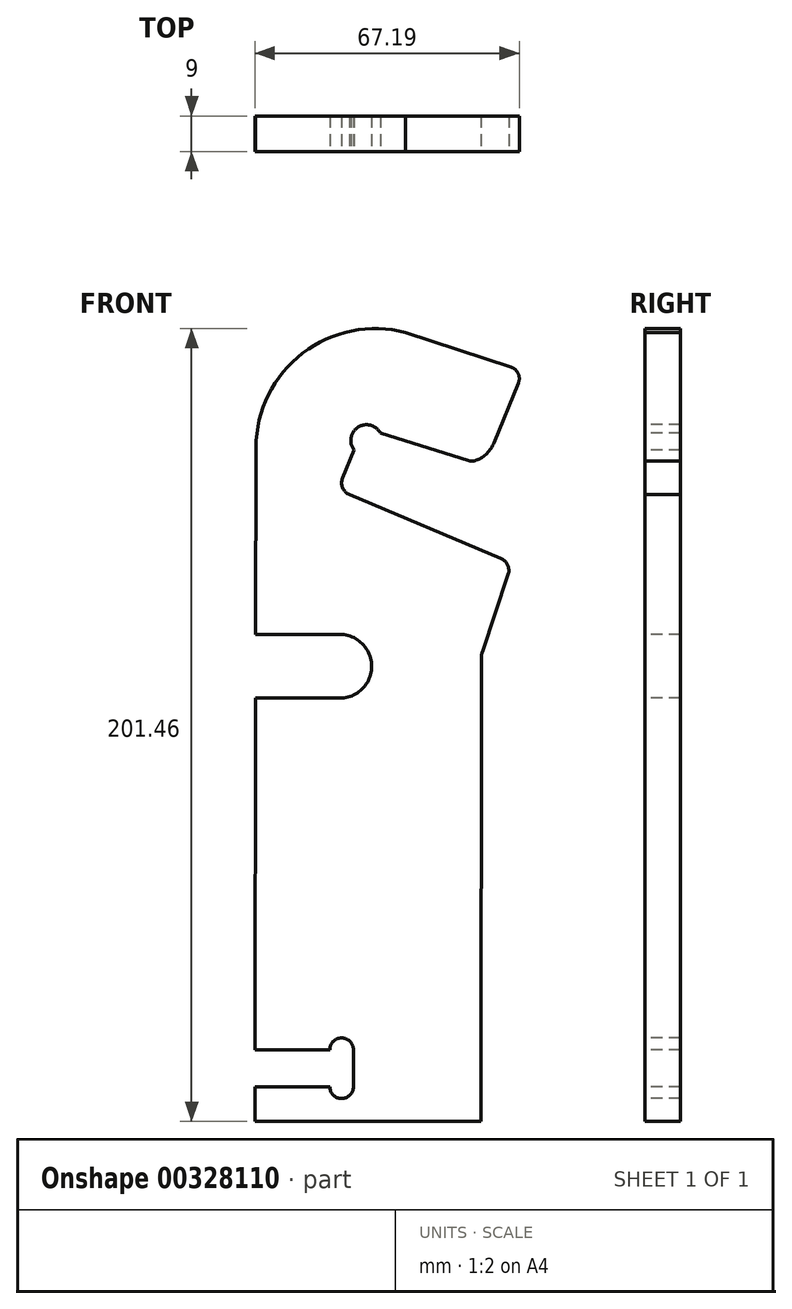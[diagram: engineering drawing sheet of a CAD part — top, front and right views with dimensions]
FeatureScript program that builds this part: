
annotation { "Feature Type Name" : "Feature", "Feature Type Description" : "" }
export const myFeature = defineFeature(function(context is Context, id is Id, definition is map)
    precondition{}
    {
        {
            var Q0;
            Q0=qCreatedBy(makeId("Front.planeOp"),FACE);
            var sketch = newSketch(context, id + "F0", { "sketchPlane" : qUnion([Q0])});
            skArc(sketch, "E0", {"start": v(12.26, 34.16) * mm, "mid": v(20.35, 26.05) * mm, "end": v(12.24, 17.96) * mm});
            skLineSegment(sketch, "E1", {"start": v(12.24, 17.96) * mm, "end": v(-9.16, 17.99) * mm});
            skLineSegment(sketch, "E2", {"start": v(-9.16, 17.99) * mm, "end": v(-9.32, -89.52) * mm});
            skLineSegment(sketch, "E3", {"start": v(-9.32, -89.52) * mm, "end": v(48.13, -89.6) * mm});
            skLineSegment(sketch, "E4", {"start": v(48.13, -89.6) * mm, "end": v(48.3, 28.7) * mm});
            skArc(sketch, "E5", {"start": v(48.3, 28.7) * mm, "mid": v(48.34, 29.2) * mm, "end": v(48.46, 29.7) * mm});
            skLineSegment(sketch, "E6", {"start": v(48.46, 29.7) * mm, "end": v(55.05, 49.38) * mm});
            skArc(sketch, "E7", {"start": v(55.05, 49.38) * mm, "mid": v(54.93, 51.79) * mm, "end": v(53.2, 53.47) * mm});
            skLineSegment(sketch, "E8", {"start": v(53.2, 53.47) * mm, "end": v(14.74, 69.69) * mm});
            skArc(sketch, "E9", {"start": v(14.74, 69.69) * mm, "mid": v(13, 71.4) * mm, "end": v(12.98, 73.86) * mm});
            skLineSegment(sketch, "E10", {"start": v(12.98, 73.86) * mm, "end": v(15.89, 81.01) * mm});
            skArc(sketch, "E11", {"start": v(15.89, 81.01) * mm, "mid": v(16.94, 86.81) * mm, "end": v(22.63, 85.27) * mm});
            skLineSegment(sketch, "E12", {"start": v(22.63, 85.27) * mm, "end": v(45.01, 78.33) * mm});
            skArc(sketch, "E13", {"start": v(45.01, 78.33) * mm, "mid": v(46.01, 78.2) * mm, "end": v(47, 78.4) * mm});
            skArc(sketch, "E14", {"start": v(47, 78.4) * mm, "mid": v(49.69, 80.16) * mm, "end": v(51.47, 82.83) * mm});
            skLineSegment(sketch, "E15", {"start": v(51.47, 82.83) * mm, "end": v(57.65, 98.06) * mm});
            skArc(sketch, "E16", {"start": v(57.65, 98.06) * mm, "mid": v(57.6, 100.45) * mm, "end": v(55.81, 102.04) * mm});
            skLineSegment(sketch, "E17", {"start": v(55.81, 102.04) * mm, "end": v(29, 110.89) * mm});
            skArc(sketch, "E18", {"start": v(29, 110.89) * mm, "mid": v(2.86, 105.6) * mm, "end": v(-9.04, 81.71) * mm});
            skLineSegment(sketch, "E19", {"start": v(-9.04, 81.71) * mm, "end": v(-9.14, 34.19) * mm});
            skLineSegment(sketch, "E20", {"start": v(-9.14, 34.19) * mm, "end": v(12.26, 34.16) * mm});
            skLineSegment(sketch, "E21", {"start": v(-19.3, -76.73) * mm, "end": v(-19.3, -75.33) * mm});
            skArc(sketch, "E22", {"start": v(-19.3, -75.33) * mm, "mid": v(-18.12, -72.5) * mm, "end": v(-15.3, -71.33) * mm});
            skLineSegment(sketch, "E23", {"start": v(-15.3, -71.33) * mm, "end": v(9.74, -71.37) * mm});
            skArc(sketch, "E24", {"start": v(9.74, -71.37) * mm, "mid": v(12.75, -68.37) * mm, "end": v(15.74, -71.38) * mm});
            skLineSegment(sketch, "E25", {"start": v(15.74, -71.38) * mm, "end": v(15.73, -80.78) * mm});
            skArc(sketch, "E26", {"start": v(15.73, -80.78) * mm, "mid": v(12.72, -83.77) * mm, "end": v(9.73, -80.77) * mm});
            skLineSegment(sketch, "E27", {"start": v(9.73, -80.77) * mm, "end": v(-15.3, -80.73) * mm});
            skArc(sketch, "E28", {"start": v(-15.3, -80.73) * mm, "mid": v(-18.13, -79.56) * mm, "end": v(-19.3, -76.73) * mm});
            skLineSegment(sketch, "E29", {"start": v(39.17, -62.62) * mm, "end": v(30.17, -62.6) * mm});
            skArc(sketch, "E30", {"start": v(30.17, -62.6) * mm, "mid": v(27, -59.42) * mm, "end": v(30.18, -56.25) * mm});
            skLineSegment(sketch, "E31", {"start": v(30.18, -56.25) * mm, "end": v(30.3, 31.05) * mm});
            skArc(sketch, "E32", {"start": v(30.3, 31.05) * mm, "mid": v(27.13, 34.23) * mm, "end": v(30.31, 37.4) * mm});
            skLineSegment(sketch, "E33", {"start": v(30.31, 37.4) * mm, "end": v(39.31, 37.38) * mm});
            skArc(sketch, "E34", {"start": v(39.31, 37.38) * mm, "mid": v(42.48, 34.2) * mm, "end": v(39.3, 31.03) * mm});
            skLineSegment(sketch, "E35", {"start": v(39.3, 31.03) * mm, "end": v(39.18, -56.27) * mm});
            skArc(sketch, "E36", {"start": v(39.18, -56.27) * mm, "mid": v(42.35, -59.45) * mm, "end": v(39.17, -62.62) * mm});
            skSolve(sketch);
        }
        {
            var Q0;
            Q0=makeQuery(id+"F0.imprint","IMPRINT",FACE,{"disambiguationData":[TD([[makeQuery(id+"F0.imprint","IMPRINT",EDGE,{"derivedFrom":sQuery(id+"F0.wireOp",EDGE,"E29")}),-1.0]])]});
            var Q1;
            {var subQ0=sQuery(id+"F0.wireOp",EDGE,"E24");Q1=makeQuery(id+"F0.imprint","IMPRINT",FACE,{"disambiguationData":[TD([[makeQuery(id+"F0.imprint","IMPRINT",EDGE,{"derivedFrom":subQ0}),-1.0]])]});}
            var Q2;
            Q2=makeQuery(id+"F0.imprint","IMPRINT",FACE,{"disambiguationData":[TD([[makeQuery(id+"F0.imprint","IMPRINT",EDGE,{"derivedFrom":sQuery(id+"F0.wireOp",EDGE,"E0")}),1.0]])]});
            extrude(context, id + "F1", {"entities" : qUnion([Q0, Q1, Q2]), "oppositeDirection" : true, "depth" : 18 * mm});
        }
        {
            var Q0;
            {var subQ0=sQuery(id+"F0.wireOp",EDGE,"E24");Q0=makeQuery(id+"F0.imprint","IMPRINT",FACE,{"disambiguationData":[TD([[makeQuery(id+"F0.imprint","IMPRINT",EDGE,{"derivedFrom":subQ0}),-1.0]])]});}
            var Q1;
            Q1=makeQuery(id+"F0.imprint","IMPRINT",FACE,{"disambiguationData":[TD([[makeQuery(id+"F0.imprint","IMPRINT",EDGE,{"derivedFrom":sQuery(id+"F0.wireOp",EDGE,"E29")}),-1.0]])]});
            extrude(context, id + "F2", {"entities" : qUnion([Q0, Q1]), "operationType" : NewBodyOperationType.REMOVE, "oppositeDirection" : true, "depth" : 9 * mm});
        }
    });
